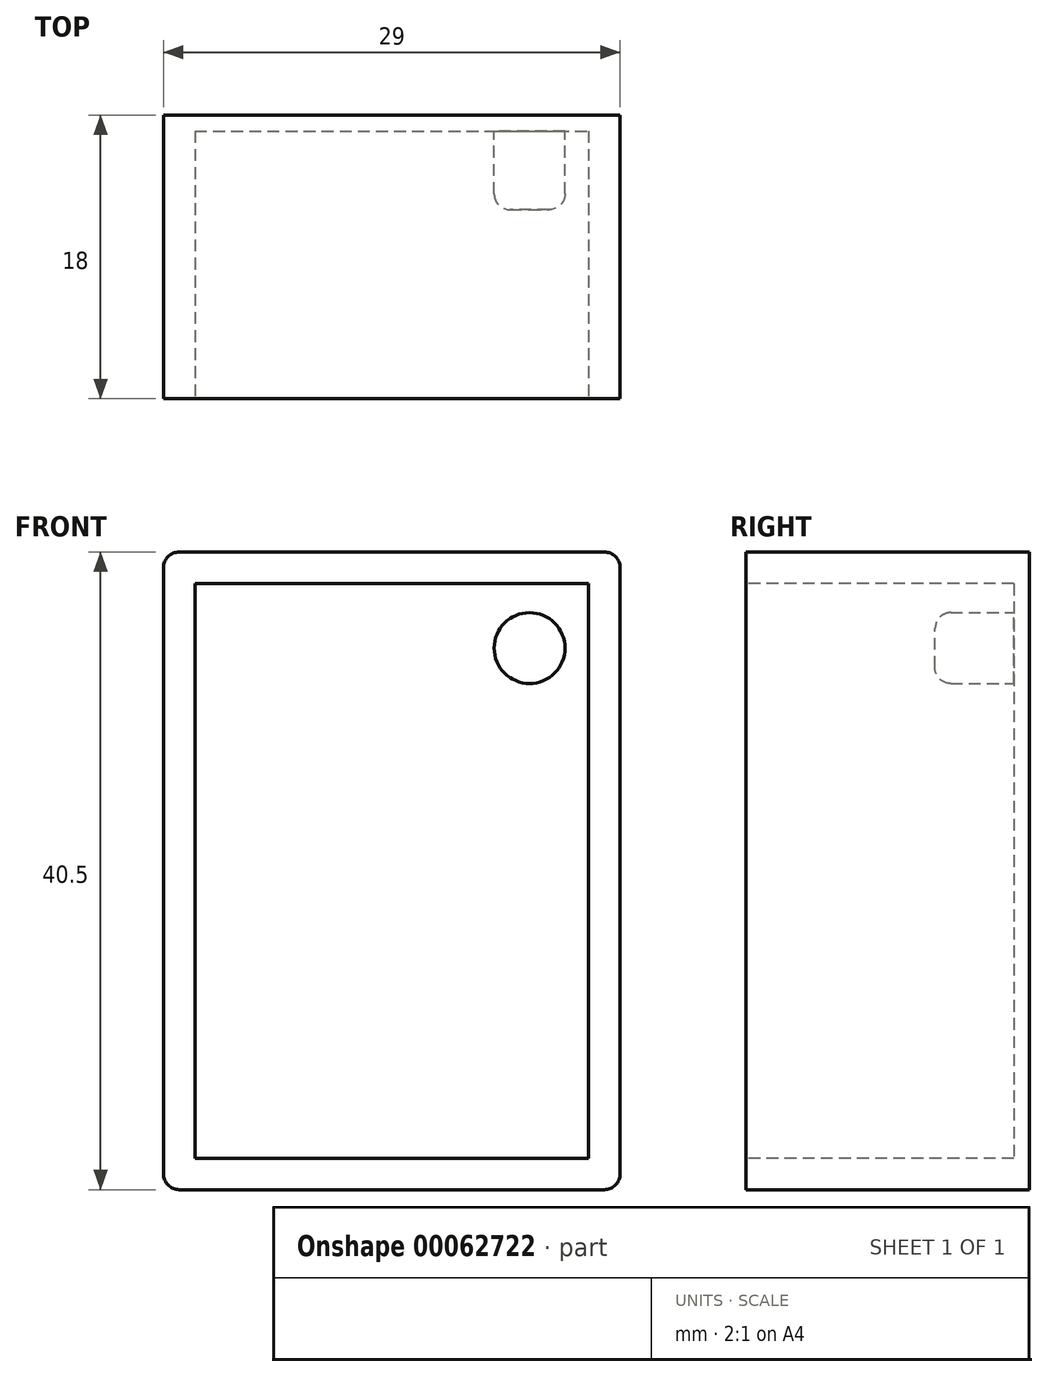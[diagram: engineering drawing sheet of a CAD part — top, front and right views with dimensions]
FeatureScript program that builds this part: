
annotation { "Feature Type Name" : "Feature", "Feature Type Description" : "" }
export const myFeature = defineFeature(function(context is Context, id is Id, definition is map)
    precondition{}
    {
        {
            var Q0;
            Q0=qCreatedBy(makeId("Front.planeOp"),FACE);
            var sketch = newSketch(context, id + "F0", { "sketchPlane" : qUnion([Q0])});
            skLineSegment(sketch, "E0.bottom", {"start": v(0, 40.5) * mm, "end": v(29, 40.5) * mm});
            skLineSegment(sketch, "E0.top", {"start": v(0, 0) * mm, "end": v(29, 0) * mm});
            skLineSegment(sketch, "E0.left", {"start": v(0, 40.5) * mm, "end": v(0, 0) * mm});
            skLineSegment(sketch, "E0.right", {"start": v(29, 40.5) * mm, "end": v(29, 0) * mm});
            skSolve(sketch);
        }
        {
            var Q0;
            Q0 = qSketchRegion(id + "F0", true);
            extrude(context, id + "F1", {"entities" : qUnion([Q0]), "depth" : 18 * mm});
        }
        {
            var Q0;
            Q0=makeQuery(id+"F1.opExtrude","CAP_FACE",FACE,{"disambiguationData":[OSD([sQuery(id+"F0.wireOp",EDGE,"E0.bottom"),sQuery(id+"F0.wireOp",EDGE,"E0.top"),sQuery(id+"F0.wireOp",EDGE,"E0.left"),sQuery(id+"F0.wireOp",EDGE,"E0.right")])],"isStart":false});
            var sketch = newSketch(context, id + "F2", { "sketchPlane" : qUnion([Q0])});
            skLineSegment(sketch, "E1.bottom", {"start": v(2, 38.5) * mm, "end": v(27, 38.5) * mm});
            skLineSegment(sketch, "E1.top", {"start": v(2, 2) * mm, "end": v(27, 2) * mm});
            skLineSegment(sketch, "E1.left", {"start": v(2, 38.5) * mm, "end": v(2, 2) * mm});
            skLineSegment(sketch, "E1.right", {"start": v(27, 38.5) * mm, "end": v(27, 2) * mm});
            skLineSegment(sketch, "E2", {"start": v(27, 38.5) * mm, "end": v(29, 40.5) * mm, "construction": true});
            skLineSegment(sketch, "E3", {"start": v(0, 40.5) * mm, "end": v(2, 38.5) * mm, "construction": true});
            skLineSegment(sketch, "E4", {"start": v(0, 0) * mm, "end": v(2, 2) * mm, "construction": true});
            skLineSegment(sketch, "E5", {"start": v(29, 0) * mm, "end": v(27, 2) * mm, "construction": true});
            skSolve(sketch);
        }
        {
            var Q0;
            Q0 = qSketchRegion(id + "F2", true);
            extrude(context, id + "F3", {"entities" : qUnion([Q0]), "operationType" : NewBodyOperationType.REMOVE, "oppositeDirection" : true, "depth" : 17 * mm});
        }
        {
            var Q0;
            Q0=makeQuery(id+"F1.opExtrude","SWEPT_FACE",FACE,{"disambiguationData":[OSD([sQuery(id+"F0.wireOp",EDGE,"E0.top")])]});
            var sketch = newSketch(context, id + "F4", { "sketchPlane" : qUnion([Q0])});
            skCircle(sketch, "E6", {"center": v(7.23, 12.78) * mm, "radius": 3 * mm});
            skCircle(sketch, "E7", {"center": v(22.05, 12.78) * mm, "radius": 3 * mm});
            skLineSegment(sketch, "E8", {"start": v(7.23, 12.78) * mm, "end": v(22.05, 12.78) * mm, "construction": true});
            skSolve(sketch);
        }
        {
            var Q0;
            Q0=makeQuery(id+"F3.boolean.opBoolean","COPY",FACE,{"derivedFrom":makeQuery(id+"F3.opExtrude","CAP_FACE",FACE,{"disambiguationData":[OSD([sQuery(id+"F2.wireOp",EDGE,"E1.bottom"),sQuery(id+"F2.wireOp",EDGE,"E1.top"),sQuery(id+"F2.wireOp",EDGE,"E1.left"),sQuery(id+"F2.wireOp",EDGE,"E1.right")])],"isStart":false})});
            var sketch = newSketch(context, id + "F5", { "sketchPlane" : qUnion([Q0])});
            skCircle(sketch, "E9", {"center": v(23.25, 34.4) * mm, "radius": 2.25 * mm});
            skSolve(sketch);
        }
        {
            var Q0;
            Q0=makeQuery(id+"F5.imprint","IMPRINT",FACE,{"disambiguationData":[TD([[makeQuery(id+"F5.imprint","IMPRINT",EDGE,{"derivedFrom":sQuery(id+"F5.wireOp",EDGE,"E9")}),1.0]])]});
            extrude(context, id + "F6", {"entities" : qUnion([Q0]), "operationType" : NewBodyOperationType.ADD, "depth" : 5 * mm});
        }
        {
            var Q0;
            Q0=makeQuery(id+"F1.opExtrude","SWEPT_EDGE",EDGE,{"disambiguationData":[OSD([sQuery(id+"F0.wireOp",EDGE,"E0.top"),sQuery(id+"F0.wireOp",EDGE,"E0.left")])]});
            var Q1;
            Q1=makeQuery(id+"F1.opExtrude","SWEPT_EDGE",EDGE,{"disambiguationData":[OSD([sQuery(id+"F0.wireOp",EDGE,"E0.top"),sQuery(id+"F0.wireOp",EDGE,"E0.right")])]});
            var Q2;
            Q2=makeQuery(id+"F1.opExtrude","SWEPT_EDGE",EDGE,{"disambiguationData":[OSD([sQuery(id+"F0.wireOp",EDGE,"E0.bottom"),sQuery(id+"F0.wireOp",EDGE,"E0.left")])]});
            var Q3;
            Q3=makeQuery(id+"F1.opExtrude","SWEPT_EDGE",EDGE,{"disambiguationData":[OSD([sQuery(id+"F0.wireOp",EDGE,"E0.bottom"),sQuery(id+"F0.wireOp",EDGE,"E0.right")])]});
            fillet(context, id + "F7", {"entities" : qUnion([Q0, Q1, Q2, Q3]), "radius" : 1 * mm, "tangentPropagation" : true, "allowEdgeOverflow" : false});
        }
        {
            var Q0;
            Q0=makeQuery(id+"F6.opExtrude","CAP_EDGE",EDGE,{"disambiguationData":[OSD([sQuery(id+"F5.wireOp",EDGE,"E9")])],"isStart":false});
            fillet(context, id + "F8", {"entities" : qUnion([Q0]), "radius" : 1 * mm, "tangentPropagation" : true, "allowEdgeOverflow" : false});
        }
    });
